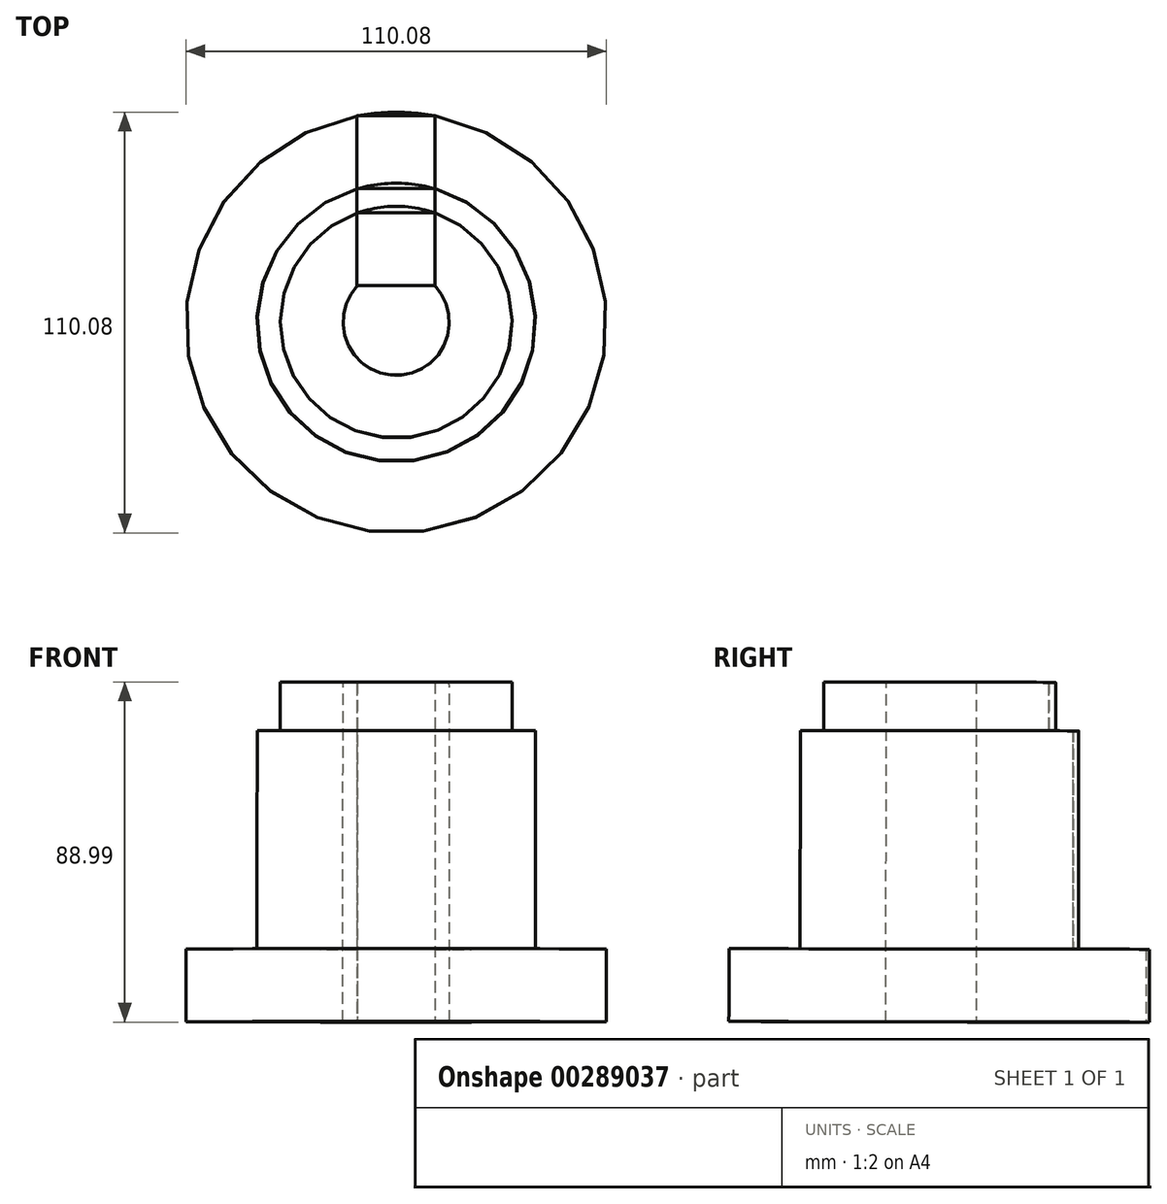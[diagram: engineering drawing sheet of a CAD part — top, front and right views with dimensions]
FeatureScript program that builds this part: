
annotation { "Feature Type Name" : "Feature", "Feature Type Description" : "" }
export const myFeature = defineFeature(function(context is Context, id is Id, definition is map)
    precondition{}
    {
        {
            var Q0;
            Q0=qCreatedBy(makeId("Top.planeOp"),FACE);
            var sketch = newSketch(context, id + "F0", { "sketchPlane" : qUnion([Q0])});
            skLineSegment(sketch, "E0.bottom", {"start": v(-7.42, 0) * mm, "end": v(-27.83, 0) * mm});
            skLineSegment(sketch, "E0.top", {"start": v(-7.42, 44.45) * mm, "end": v(-27.83, 44.45) * mm});
            skLineSegment(sketch, "E0.left", {"start": v(-7.42, 0) * mm, "end": v(-7.42, 44.45) * mm});
            skLineSegment(sketch, "E0.right", {"start": v(-27.83, 0) * mm, "end": v(-27.83, 19.05) * mm});
            skLineSegment(sketch, "E1", {"start": v(-27.83, 19.05) * mm, "end": v(-7.42, 19.05) * mm});
            skLineSegment(sketch, "E2", {"start": v(-27.83, 25.4) * mm, "end": v(-7.42, 25.4) * mm});
            skLineSegment(sketch, "E3", {"start": v(-27.83, 19.05) * mm, "end": v(-27.83, 25.4) * mm});
            skLineSegment(sketch, "E4", {"start": v(-27.83, 25.4) * mm, "end": v(-27.83, 44.45) * mm});
            skLineSegment(sketch, "E5", {"start": v(-17.63, 0) * mm, "end": v(-17.63, -9.52) * mm, "construction": true});
            skSolve(sketch);
        }
        {
            var Q0;
            {var subQ0=sQuery(id+"F0.wireOp",EDGE,"E0.top");Q0=makeQuery(id+"F0.imprint","IMPRINT",FACE,{"disambiguationData":[TD([[makeQuery(id+"F0.imprint","IMPRINT",EDGE,{"derivedFrom":subQ0}),1.0]])]});}
            var Q1;
            {var subQ0=sQuery(id+"F0.wireOp",EDGE,"E1");Q1=makeQuery(id+"F0.imprint","IMPRINT",FACE,{"disambiguationData":[TD([[makeQuery(id+"F0.imprint","IMPRINT",EDGE,{"derivedFrom":subQ0}),1.0]])]});}
            var Q2;
            {var subQ0=sQuery(id+"F0.wireOp",EDGE,"E0.bottom");Q2=makeQuery(id+"F0.imprint","IMPRINT",FACE,{"disambiguationData":[TD([[makeQuery(id+"F0.imprint","IMPRINT",EDGE,{"derivedFrom":subQ0}),-1.0]])]});}
            extrude(context, id + "F1", {"entities" : qUnion([Q0, Q1, Q2]), "depth" : 19.05 * mm});
        }
        {
            var Q0;
            Q0=makeQuery(id+"F1.opExtrude","CAP_FACE",FACE,{"disambiguationData":[OSD([sQuery(id+"F0.wireOp",EDGE,"E0.bottom"),sQuery(id+"F0.wireOp",EDGE,"E0.top"),sQuery(id+"F0.wireOp",EDGE,"E0.left"),sQuery(id+"F0.wireOp",EDGE,"E0.right"),sQuery(id+"F0.wireOp",EDGE,"E3"),sQuery(id+"F0.wireOp",EDGE,"E4")])],"isStart":false});
            var sketch = newSketch(context, id + "F2", { "sketchPlane" : qUnion([Q0])});
            skLineSegment(sketch, "E6.bottom", {"start": v(-27.83, 0) * mm, "end": v(-7.42, 0) * mm});
            skLineSegment(sketch, "E6.top", {"start": v(-27.83, 25.4) * mm, "end": v(-7.42, 25.4) * mm});
            skLineSegment(sketch, "E6.left", {"start": v(-27.83, 0) * mm, "end": v(-27.83, 25.4) * mm});
            skLineSegment(sketch, "E6.right", {"start": v(-7.42, 0) * mm, "end": v(-7.42, 25.4) * mm});
            skSolve(sketch);
        }
        {
            var Q0;
            Q0=makeQuery(id+"F2.imprint","IMPRINT",FACE,{"disambiguationData":[TD([[makeQuery(id+"F2.imprint","IMPRINT",EDGE,{"derivedFrom":sQuery(id+"F2.wireOp",EDGE,"E6.bottom")}),-1.0]])]});
            extrude(context, id + "F3", {"entities" : qUnion([Q0]), "operationType" : NewBodyOperationType.ADD, "depth" : 57.15 * mm});
        }
        {
            var Q0;
            Q0=makeQuery(id+"F3.opExtrude","CAP_FACE",FACE,{"disambiguationData":[OSD([sQuery(id+"F2.wireOp",EDGE,"E6.bottom"),sQuery(id+"F2.wireOp",EDGE,"E6.top"),sQuery(id+"F2.wireOp",EDGE,"E6.left"),sQuery(id+"F2.wireOp",EDGE,"E6.right")])],"isStart":false});
            var sketch = newSketch(context, id + "F4", { "sketchPlane" : qUnion([Q0])});
            skLineSegment(sketch, "E7.bottom", {"start": v(-27.83, 0) * mm, "end": v(-7.42, 0) * mm});
            skLineSegment(sketch, "E7.top", {"start": v(-27.83, 19.05) * mm, "end": v(-7.42, 19.05) * mm});
            skLineSegment(sketch, "E8.bottom", {"start": v(-27.83, 0) * mm, "end": v(-7.42, 0) * mm, "construction": true});
            skLineSegment(sketch, "E8.left", {"start": v(-27.83, 0) * mm, "end": v(-27.83, 0) * mm});
            skLineSegment(sketch, "E8.right", {"start": v(-7.42, 0) * mm, "end": v(-7.42, 0) * mm});
            skLineSegment(sketch, "E9", {"start": v(-27.83, 0) * mm, "end": v(-27.83, 19.05) * mm});
            skLineSegment(sketch, "E10", {"start": v(-7.42, 0) * mm, "end": v(-7.42, 19.05) * mm});
            skSolve(sketch);
        }
        {
            var Q0;
            Q0=makeQuery(id+"F4.imprint","IMPRINT",FACE,{"disambiguationData":[TD([[makeQuery(id+"F4.imprint","IMPRINT",EDGE,{"derivedFrom":sQuery(id+"F4.wireOp",EDGE,"E7.bottom")}),-1.0]])]});
            extrude(context, id + "F5", {"entities" : qUnion([Q0]), "operationType" : NewBodyOperationType.ADD, "depth" : 12.7 * mm});
        }
        {
            var Q0;
            {var subQ0=sQuery(id+"F4.wireOp",EDGE,"E7.left");Q0=makeQuery(id+"FKZgPb401PDbjmH_1.boolean.opBoolean","MERGE",FACE,{"derivedFrom":[makeQuery(id+"F5.opExtrude","CAP_FACE",FACE,{"disambiguationData":[OSD([sQuery(id+"F4.wireOp",EDGE,"E7.bottom"),sQuery(id+"F4.wireOp",EDGE,"E7.top"),subQ0,sQuery(id+"F4.wireOp",EDGE,"E7.right")])],"isStart":false}),makeQuery(id+"FKZgPb401PDbjmH_1.opRevolve","SWEPT_FACE",FACE,{"disambiguationData":[OSD([subQ0])]})]});}
            var sketch = newSketch(context, id + "F6", { "sketchPlane" : qUnion([Q0])});
            skCircle(sketch, "E11", {"center": v(-17.63, -9.52) * mm, "radius": 9.53 * mm, "construction": true});
            skLineSegment(sketch, "E12", {"start": v(-17.63, -9.52) * mm, "end": v(-17.63, 0) * mm, "construction": true});
            skPoint(sketch, "E12.endSnap0", {"position": v(-17.63, 0) * mm});
            skSolve(sketch);
        }
        {
            var Q0;
            Q0=makeQuery(id+"F1.opExtrude","CAP_FACE",FACE,{"disambiguationData":[OSD([sQuery(id+"F0.wireOp",EDGE,"E0.bottom"),sQuery(id+"F0.wireOp",EDGE,"E0.top"),sQuery(id+"F0.wireOp",EDGE,"E0.left"),sQuery(id+"F0.wireOp",EDGE,"E0.right"),sQuery(id+"F0.wireOp",EDGE,"E3"),sQuery(id+"F0.wireOp",EDGE,"E4")])],"isStart":true});
            var sketch = newSketch(context, id + "F7", { "sketchPlane" : qUnion([Q0])});
            skPoint(sketch, "E13.endSnap0", {"position": v(-12.73, -5.03) * mm});
            skCircle(sketch, "E14", {"center": v(-17.73, 9.65) * mm, "radius": 9.53 * mm, "construction": true});
            skLineSegment(sketch, "E15", {"start": v(-17.73, 9.65) * mm, "end": v(-17.73, 19.18) * mm, "construction": true});
            skPoint(sketch, "E15.endSnap0", {"position": v(-17.73, 19.18) * mm});
            skLineSegment(sketch, "E16", {"start": v(-17.73, 9.65) * mm, "end": v(-8.2, 9.65) * mm, "construction": true});
            skLineSegment(sketch, "E17", {"start": v(-8.2, 9.65) * mm, "end": v(10.1, 9.65) * mm, "construction": true});
            skSolve(sketch);
        }
        {
            var Q0;
            Q0=sQuery(id+"F6.wireOp",VERTEX,"E11.center");
            var Q1;
            Q1=sQuery(id+"F7.wireOp",VERTEX,"E15.start");
            var Q2;
            Q2=sQuery(id+"F7.wireOp",VERTEX,"E17.start");
            cPlane(context, id + "F8", {"entities" : qUnion([Q0, Q1, Q2]), "cplaneType" : CPlaneType.THREE_POINT, "offset" : 25.4 * mm, "width" : 152.4 * mm, "height" : 152.4 * mm});
        }
        {
            var Q0;
            Q0=qCreatedBy(id+"F8.planeOp",FACE);
            var sketch = newSketch(context, id + "F9", { "sketchPlane" : qUnion([Q0])});
            skLineSegment(sketch, "E18", {"start": v(17.54, 88.95) * mm, "end": v(17.54, -2.95) * mm, "construction": true});
            skSolve(sketch);
        }
        {
            var Q0;
            Q0=makeQuery(id+"F5.boolean.opBoolean","MERGE",FACE,{"derivedFrom":[makeQuery(id+"F3.boolean.opBoolean","MERGE",FACE,{"derivedFrom":[makeQuery(id+"F1.opExtrude","SWEPT_FACE",FACE,{"disambiguationData":[OSD([sQuery(id+"F0.wireOp",EDGE,"E0.left")])]}),makeQuery(id+"F3.opExtrude","SWEPT_FACE",FACE,{"disambiguationData":[OSD([sQuery(id+"F2.wireOp",EDGE,"E6.right")])]})]}),makeQuery(id+"F5.opExtrude","SWEPT_FACE",FACE,{"disambiguationData":[OSD([sQuery(id+"F4.wireOp",EDGE,"E10")])]})]});
            var Q1;
            Q1=sQuery(id+"F9.wireOp",EDGE,"E18");
            revolve(context, id + "F10", {"operationType" : NewBodyOperationType.ADD, "entities" : qUnion([Q0]), "axis" : qUnion([Q1]), "revolveType" : RevolveType.FULL});
        }
    });
